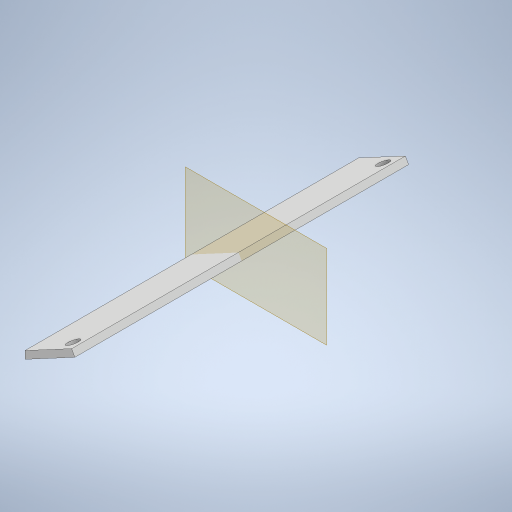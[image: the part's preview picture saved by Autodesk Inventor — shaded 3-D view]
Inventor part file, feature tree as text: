
AUTODESK INVENTOR PART (.ipt)
format: ipt  version: 2023 (Build 270158000, 158)  size: 306,688 bytes
history: native  units: in
note: dims shown in document units (in); Inventor stores cm internally (conversion verified against a paired STEP export)
features: other x9, reference x9, extrude x5, sketch x5, projected_geometry x3, mirror x1
ambient origin geometry x8: Origin, YZ Plane, XZ Plane, XY Plane, X Axis, Y Axis, Z Axis, Center Point
bodies: Body1 (feature_tree)
feature tree (32):
  other  "Bryła1"
  extrude  "Wyciągnięcie proste1"  Depth=3.937in
  extrude  "Wyciągnięcie proste4"  Depth=3.937in TaperAngle=0.0deg
  other  "Płaszczyzna konstrukcyjna1"
  mirror  "Odbij1"
  extrude  "Wyciągnięcie proste5"  Depth=0.0197in
  extrude  "Wyciągnięcie proste6"  Depth=0.0197in
  extrude  "Wyciągnięcie proste7"  Depth=0.3937in TaperAngle=0.0deg
  sketch  "Szkic1"
  reference  "Odniesienie1"
  reference  "Odniesienie2"
  reference  "Odniesienie3"
  reference  "Odniesienie4"
  sketch  "Szkic5"
  reference  "Odniesienie15"
  reference  "Odniesienie16"
  reference  "Odniesienie17"
  sketch  "Szkic6"
  reference  "Odniesienie18"
  reference  "Odniesienie19"
  sketch  "Szkic7"
  projected_geometry  "Pętla rzutowana3"
  sketch  "Szkic8"
  projected_geometry  "Pętla rzutowana4"
  projected_geometry  "Pętla rzutowana5"
  other  "<userpath>\Desktop\MojeRoboty\Stefan\mechanics 2\STEFAN.iam"
  other  "STEFAN.iam"
  other  "podstawa:1"
  other  "koło_minisumo:2"
  other  "plug_nowy:1"
  other  "mocowanie sharpow:1"
  other  "plug_2:1"
